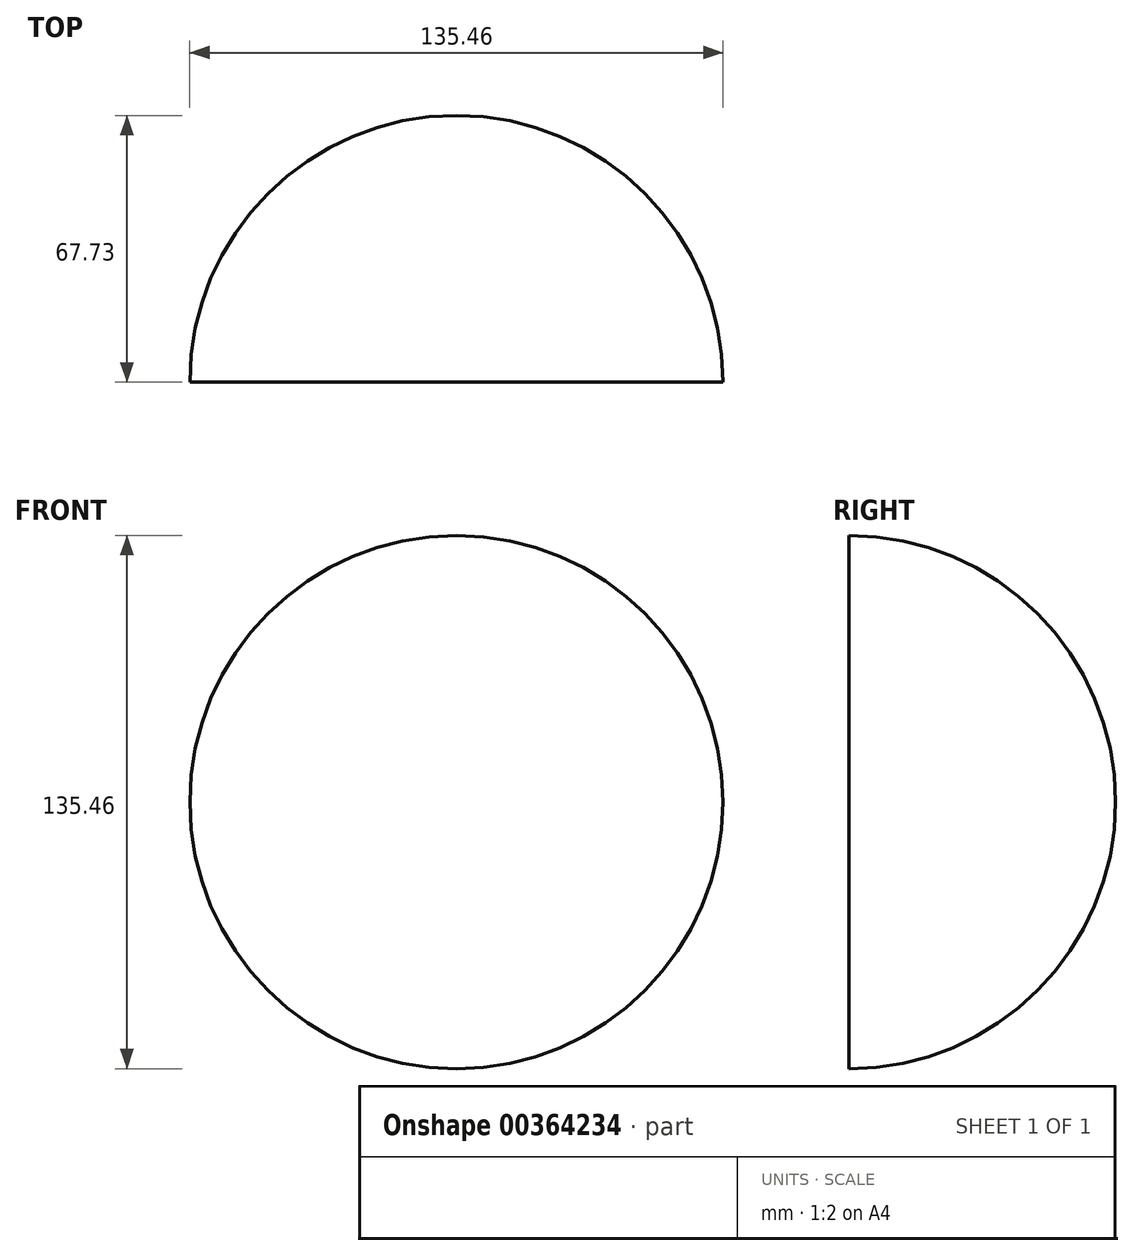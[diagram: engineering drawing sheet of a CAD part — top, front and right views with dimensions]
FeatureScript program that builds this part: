
annotation { "Feature Type Name" : "Feature", "Feature Type Description" : "" }
export const myFeature = defineFeature(function(context is Context, id is Id, definition is map)
    precondition{}
    {
        {
            var Q0;
            Q0=qCreatedBy(makeId("Front.planeOp"),FACE);
            var sketch = newSketch(context, id + "F0", { "sketchPlane" : qUnion([Q0])});
            skCircle(sketch, "E0", {"center": v(0, 0) * mm, "radius": 67.73 * mm});
            skLineSegment(sketch, "E1", {"start": v(0, 67.73) * mm, "end": v(0, -67.73) * mm});
            skPoint(sketch, "E2", {"position": v(-67.73, 0) * mm});
            skPoint(sketch, "E3", {"position": v(0, -67.73) * mm});
            skPoint(sketch, "E4", {"position": v(0, 67.73) * mm});
            skSolve(sketch);
        }
        {
            var Q0;
            {var subQ0=sQuery(id+"F0.wireOp",EDGE,"E1");Q0=makeQuery(id+"F0.imprint","IMPRINT",FACE,{"disambiguationData":[TD([[makeQuery(id+"F0.imprint","IMPRINT",EDGE,{"derivedFrom":subQ0}),-1.0]])]});}
            var Q1;
            Q1=sQuery(id+"F0.wireOp",EDGE,"E1");
            revolve(context, id + "F1", {"entities" : qUnion([Q0]), "axis" : qUnion([Q1]), "revolveType" : RevolveType.ONE_DIRECTION, "angle" : 180 * degree});
        }
    });
